# Revit family: Multi_Sport_Cage-PSS-4080
name_source: partatom
category: Specialty Equipment
revit_build: Autodesk Revit 2017 (Build: 20170816_0615(x64)
units: mm (PartAtom-declared; Revit-internal decimal feet)

## family parameters
Always vertical = Yes
Cut with Voids When Loaded = No
OmniClass Number = 23.40.50.34.14
OmniClass Title = Gymnasium Equipment
Part Type = Normal
Room Calculation Point = No
Round Connector Dimension = Use Diameter
Shared = No
Work Plane-Based = No

## types (2) — shared parameters
Assembly Code = E1020900
Attachment Height = 24' - 6"
Bridge Pipe Requirement = If Structure exceeds 14' span
CSI MasterFormat = 11 66 23
Carrier Center Spacing = 12' - 0"
Description = Multi-Sport Cage, Ceiling-Hung
Dim End to First Carriers = 1' - 6"
Height = 10' - 0"
Manufacturer = Performance Sports Systems
Maximum Size Limitations = Contact PSS
Model = 4080
Product Page URL = http://www.perfsports.com
Superstructure Finish = Powder Coat - Performance Sports Systems - Black
URL = http://www.perfsports.com
Width = 12' - 0"

## per-type parameters (varying)
| type | BIM Version | Length |
| 70'-0" x 12'-0" x 10'-0" | v3.1 | 70' - 0" |
| 55'-0" x 12'-0" x 10'-0" | v1.1 | 54' - 0" |

## geometry (parser evidence)
native form markers: Blend x27, Sweep x10
no freeform markers — native parametric forms only
